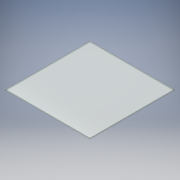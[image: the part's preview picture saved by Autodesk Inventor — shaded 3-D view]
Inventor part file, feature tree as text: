
AUTODESK INVENTOR PART (.ipt)
format: ipt  version: 2019 (Build 230136000, 136)  size: 95,232 bytes
history: native  units: mm
features: other x1, extrude x1, sketch x1
ambient origin geometry x8: Origin, YZ Plane, XZ Plane, XY Plane, X Axis, Y Axis, Z Axis, Center Point
bodies: Body1 (feature_tree)
feature tree (3):
  other  "Bryła1"
  extrude  "Wyciągnięcie proste1"  Depth=50.0mm
  sketch  "Szkic1"
